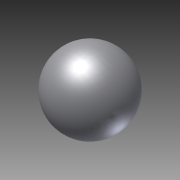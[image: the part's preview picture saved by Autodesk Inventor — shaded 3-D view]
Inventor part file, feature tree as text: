
AUTODESK INVENTOR PART (.ipt)
format: ipt  version: 2012 SP2 (Build 160219200, 219)  size: 100,352 bytes
history: native  units: in
note: dims shown in document units (in); Inventor stores cm internally (conversion verified against a paired STEP export)
features: sketch x2, reference x2, revolve x1
ambient origin geometry x8: Origin, YZ Plane, XZ Plane, XY Plane, X Axis, Y Axis, Z Axis, Center Point
bodies: Solid1 (feature_tree)
feature tree (5):
  sketch  "Sketch1"  dims[d5=90.0deg]
  revolve  "Revolution1"  [1 undecoded]
  sketch  "Sketch2"
  reference  "Reference1"
  reference  "Reference2"
note: 1 required parameter value undecoded (feature->parameter linkage not recoverable at this tier; creation-order binding heuristic only, values carry confidence <= 0.55)
